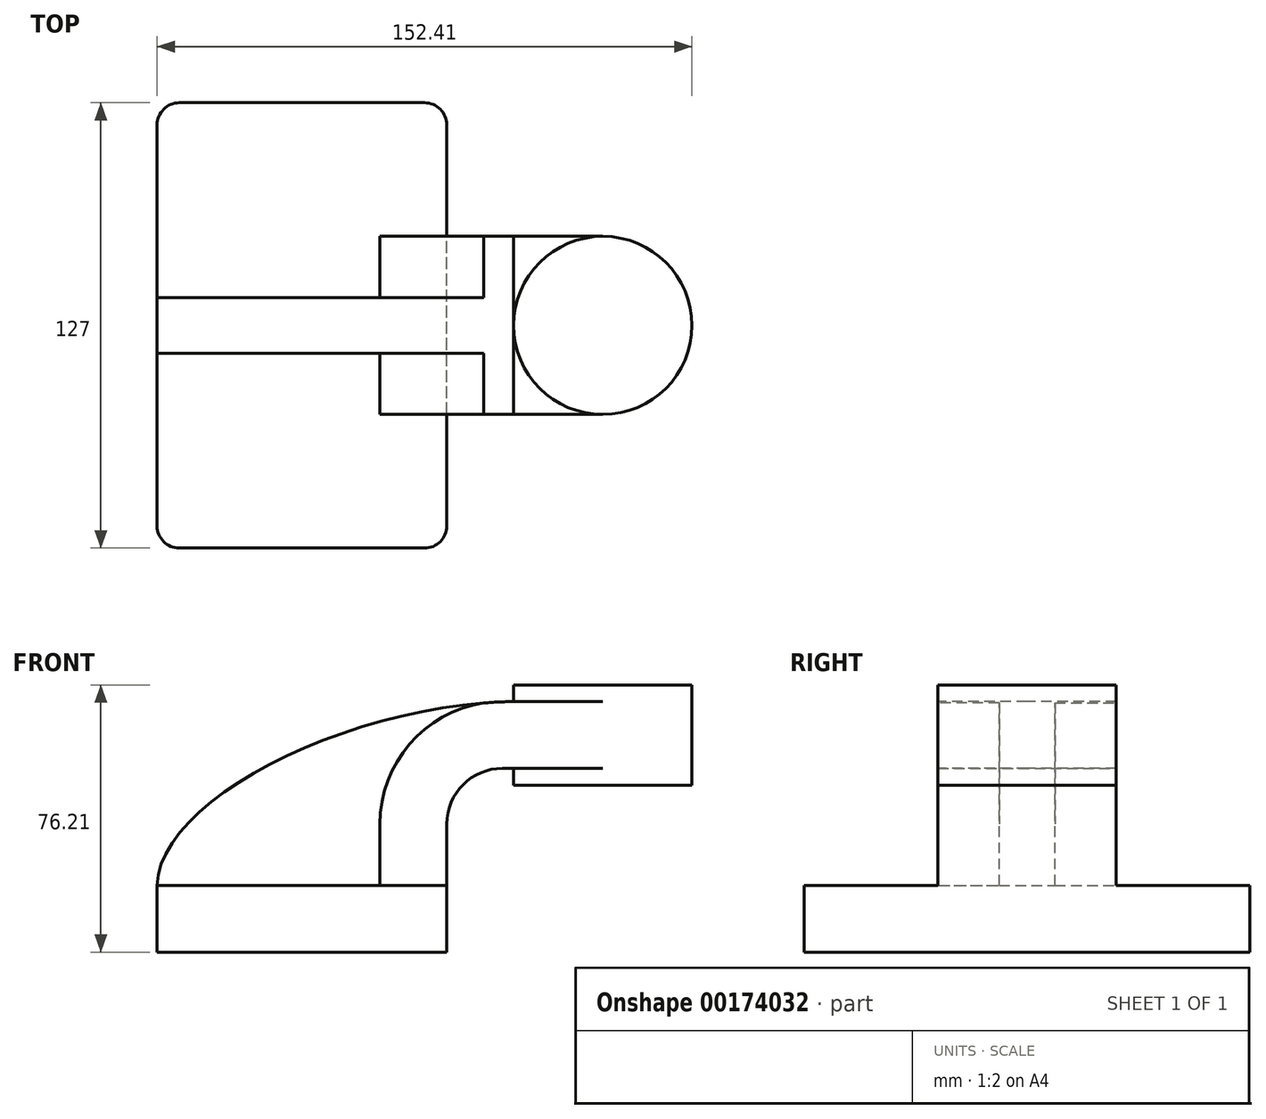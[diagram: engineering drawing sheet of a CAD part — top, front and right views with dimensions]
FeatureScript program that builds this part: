
annotation { "Feature Type Name" : "Feature", "Feature Type Description" : "" }
export const myFeature = defineFeature(function(context is Context, id is Id, definition is map)
    precondition{}
    {
        {
            var Q0;
            Q0=qCreatedBy(makeId("Front.planeOp"),FACE);
            var sketch = newSketch(context, id + "F0", { "sketchPlane" : qUnion([Q0])});
            skLineSegment(sketch, "E0.bottom", {"start": v(41.28, 9.53) * mm, "end": v(-41.28, 9.53) * mm});
            skLineSegment(sketch, "E0.top", {"start": v(41.28, -9.52) * mm, "end": v(-41.27, -9.52) * mm});
            skLineSegment(sketch, "E0.left", {"start": v(41.28, 9.53) * mm, "end": v(41.28, -9.52) * mm});
            skLineSegment(sketch, "E0.right", {"start": v(-41.28, 9.53) * mm, "end": v(-41.27, -9.52) * mm});
            skPoint(sketch, "E0.middle", {"position": v(0, 0) * mm});
            skLineSegment(sketch, "E1.bottom", {"start": v(111.13, 66.68) * mm, "end": v(60.33, 66.68) * mm});
            skLineSegment(sketch, "E1.top", {"start": v(111.13, 38.1) * mm, "end": v(60.33, 38.1) * mm});
            skLineSegment(sketch, "E1.left", {"start": v(111.13, 66.68) * mm, "end": v(111.13, 38.1) * mm});
            skLineSegment(sketch, "E1.right", {"start": v(60.33, 66.68) * mm, "end": v(60.33, 38.1) * mm});
            skPoint(sketch, "E1.middle", {"position": v(85.73, 52.39) * mm});
            skLineSegment(sketch, "E2", {"start": v(41.27, 9.53) * mm, "end": v(41.27, 27) * mm});
            skArc(sketch, "E3", {"start": v(41.28, 27) * mm, "mid": v(45.92, 38.23) * mm, "end": v(57.15, 42.88) * mm});
            skLineSegment(sketch, "E4", {"start": v(57.15, 42.88) * mm, "end": v(85.73, 42.88) * mm});
            skLineSegment(sketch, "E5.0", {"start": v(57.15, 61.93) * mm, "end": v(85.73, 61.93) * mm});
            skArc(sketch, "E5.1", {"start": v(22.23, 27) * mm, "mid": v(32.45, 51.7) * mm, "end": v(57.15, 61.93) * mm});
            skLineSegment(sketch, "E5.2", {"start": v(22.22, 9.53) * mm, "end": v(22.22, 27) * mm});
            skLineSegment(sketch, "E6", {"start": v(85.73, 38.1) * mm, "end": v(85.73, 66.68) * mm});
            skFitSpline(sketch, "E7", {"points": [v(-41.28, 9.53) * mm, v(60.33, 61.93) * mm], "startDerivative": vector(1.35, 72.9) * mm, "endDerivative": vector(142.17, 2.24) * mm});
            skSolve(sketch);
        }
        {
            var Q0;
            Q0=makeQuery(id+"F0.imprint","IMPRINT",FACE,{"disambiguationData":[TD([[makeQuery(id+"F0.imprint","IMPRINT",EDGE,{"derivedFrom":sQuery(id+"F0.wireOp",EDGE,"E0.top")}),-1.0]])]});
            extrude(context, id + "F1", {"entities" : qUnion([Q0]), "endBound" : BoundingType.SYMMETRIC, "depth" : 127 * mm});
        }
        {
            var Q0;
            {var subQ1=sQuery(id+"F0.wireOp",EDGE,"E2");Q0=makeQuery(id+"F0.imprint","IMPRINT",FACE,{"disambiguationData":[TD([[makeQuery(id+"F0.imprint","IMPRINT",EDGE,{"derivedFrom":subQ1}),1.0]])]});}
            var Q1;
            {var subQ3=sQuery(id+"F0.wireOp",EDGE,"E4");var subQ5=sQuery(id+"F0.wireOp",EDGE,"E6");var subQ6=makeQuery(id+"F0.imprint","INTERSECT",VERTEX,{"derivedFrom":[subQ3,subQ5]});Q1=makeQuery(id+"F0.imprint","IMPRINT",FACE,{"disambiguationData":[TD([[makeQuery(id+"F0.imprint","IMPRINT",EDGE,{"disambiguationData":[TD([[subQ6,1.0]])],"derivedFrom":subQ3}),1.0]])]});}
            extrude(context, id + "F2", {"entities" : qUnion([Q0, Q1]), "operationType" : NewBodyOperationType.ADD, "endBound" : BoundingType.SYMMETRIC, "depth" : 50.8 * mm});
        }
        {
            var Q0;
            {var subQ3=sQuery(id+"F0.wireOp",EDGE,"E5.2");Q0=makeQuery(id+"F0.imprint","IMPRINT",FACE,{"disambiguationData":[TD([[makeQuery(id+"F0.imprint","IMPRINT",EDGE,{"derivedFrom":subQ3}),1.0]])]});}
            extrude(context, id + "F3", {"entities" : qUnion([Q0]), "operationType" : NewBodyOperationType.ADD, "endBound" : BoundingType.SYMMETRIC, "depth" : 15.88 * mm});
        }
        {
            var Q0;
            {var subQ0=sQuery(id+"F0.wireOp",EDGE,"E1.left");Q0=makeQuery(id+"F0.imprint","IMPRINT",FACE,{"disambiguationData":[TD([[makeQuery(id+"F0.imprint","IMPRINT",EDGE,{"derivedFrom":subQ0}),-1.0]])]});}
            var Q1;
            Q1=sQuery(id+"F0.wireOp",EDGE,"E6");
            revolve(context, id + "F4", {"operationType" : NewBodyOperationType.ADD, "entities" : qUnion([Q0]), "axis" : qUnion([Q1]), "revolveType" : RevolveType.FULL});
        }
        {
            var Q0;
            Q0=makeQuery(id+"F1.opExtrude","CAP_EDGE",EDGE,{"disambiguationData":[OSD([sQuery(id+"F0.wireOp",EDGE,"E0.left")])],"isStart":false});
            var Q1;
            Q1=makeQuery(id+"F1.opExtrude","CAP_EDGE",EDGE,{"disambiguationData":[OSD([sQuery(id+"F0.wireOp",EDGE,"E0.right")])],"isStart":false});
            var Q2;
            Q2=makeQuery(id+"F1.opExtrude","CAP_EDGE",EDGE,{"disambiguationData":[OSD([sQuery(id+"F0.wireOp",EDGE,"E0.left")])],"isStart":true});
            var Q3;
            Q3=makeQuery(id+"F1.opExtrude","CAP_EDGE",EDGE,{"disambiguationData":[OSD([sQuery(id+"F0.wireOp",EDGE,"E0.right")])],"isStart":true});
            fillet(context, id + "F5", {"entities" : qUnion([Q0, Q1, Q2, Q3]), "radius" : 6.35 * mm, "tangentPropagation" : true, "allowEdgeOverflow" : false});
        }
    });
